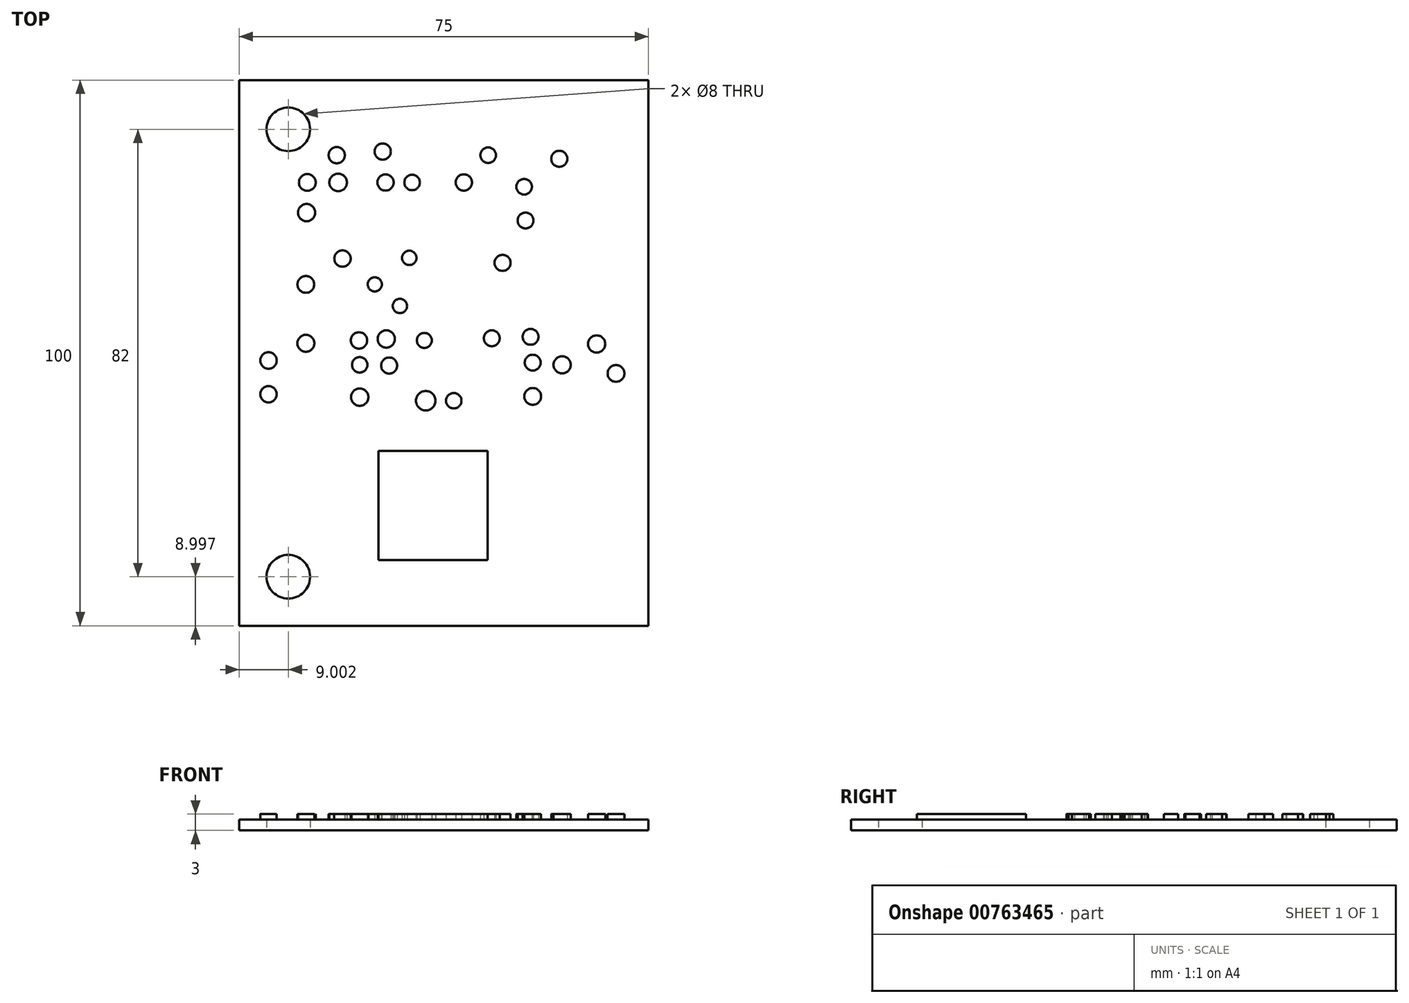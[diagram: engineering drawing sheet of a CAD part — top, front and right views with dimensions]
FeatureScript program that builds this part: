
annotation { "Feature Type Name" : "Feature", "Feature Type Description" : "" }
export const myFeature = defineFeature(function(context is Context, id is Id, definition is map)
    precondition{}
    {
        {
            var Q0;
            Q0=qCreatedBy(makeId("Top.planeOp"),FACE);
            var sketch = newSketch(context, id + "F0", { "sketchPlane" : qUnion([Q0])});
            skLineSegment(sketch, "E0.bottom", {"start": v(-62.6, 51.3) * mm, "end": v(12.4, 51.3) * mm});
            skLineSegment(sketch, "E0.top", {"start": v(-62.6, -48.7) * mm, "end": v(12.4, -48.7) * mm});
            skLineSegment(sketch, "E0.left", {"start": v(-62.6, 51.3) * mm, "end": v(-62.6, -48.7) * mm});
            skLineSegment(sketch, "E0.right", {"start": v(12.4, 51.3) * mm, "end": v(12.4, -48.7) * mm});
            skPoint(sketch, "E0.middle", {"position": v(-25.1, 1.3) * mm});
            skCircle(sketch, "E1", {"center": v(-53.6, 42.3) * mm, "radius": 4 * mm});
            skCircle(sketch, "E2", {"center": v(-53.6, -39.7) * mm, "radius": 4 * mm});
            skSolve(sketch);
        }
        {
            var Q0;
            Q0 = qSketchRegion(id + "F0", true);
            extrude(context, id + "F1", {"entities" : qUnion([Q0]), "depth" : 2 * mm, "offsetDistance" : 25 * mm});
        }
        {
            var Q0;
            Q0=makeQuery(id+"F1.opExtrude","CAP_FACE",FACE,{"disambiguationData":[OSD([sQuery(id+"F0.wireOp",EDGE,"E0.bottom"),sQuery(id+"F0.wireOp",EDGE,"E0.top"),sQuery(id+"F0.wireOp",EDGE,"E0.left"),sQuery(id+"F0.wireOp",EDGE,"E0.right"),sQuery(id+"F0.wireOp",EDGE,"E1"),sQuery(id+"F0.wireOp",EDGE,"E2")])],"isStart":false});
            var sketch = newSketch(context, id + "F2", { "sketchPlane" : qUnion([Q0])});
            skCircle(sketch, "E3", {"center": v(-44.72, 37.57) * mm, "radius": 1.49 * mm});
            skCircle(sketch, "E4", {"center": v(-44.46, 32.57) * mm, "radius": 1.6 * mm});
            skCircle(sketch, "E5", {"center": v(-50.12, 32.57) * mm, "radius": 1.53 * mm});
            skCircle(sketch, "E6", {"center": v(-50.25, 27.04) * mm, "radius": 1.58 * mm});
            skCircle(sketch, "E7", {"center": v(-30.9, 32.57) * mm, "radius": 1.42 * mm});
            skCircle(sketch, "E8", {"center": v(-35.78, 32.57) * mm, "radius": 1.49 * mm});
            skCircle(sketch, "E9", {"center": v(-36.3, 38.22) * mm, "radius": 1.49 * mm});
            skCircle(sketch, "E10", {"center": v(-21.43, 32.57) * mm, "radius": 1.5 * mm});
            skCircle(sketch, "E11", {"center": v(-16.96, 37.57) * mm, "radius": 1.42 * mm});
            skCircle(sketch, "E12", {"center": v(-10.12, 25.6) * mm, "radius": 1.45 * mm});
            skCircle(sketch, "E13", {"center": v(-10.38, 31.78) * mm, "radius": 1.42 * mm});
            skCircle(sketch, "E14", {"center": v(-3.93, 36.9) * mm, "radius": 1.47 * mm});
            skCircle(sketch, "E15", {"center": v(-50.38, 13.88) * mm, "radius": 1.53 * mm});
            skCircle(sketch, "E16", {"center": v(-43.67, 18.62) * mm, "radius": 1.5 * mm});
            skCircle(sketch, "E17", {"center": v(-33.14, 9.93) * mm, "radius": 1.32 * mm});
            skCircle(sketch, "E18", {"center": v(-37.75, 13.88) * mm, "radius": 1.3 * mm});
            skCircle(sketch, "E19", {"center": v(-31.43, 18.75) * mm, "radius": 1.32 * mm});
            skCircle(sketch, "E20", {"center": v(-14.33, 17.83) * mm, "radius": 1.47 * mm});
            skCircle(sketch, "E21", {"center": v(-57.22, -6.25) * mm, "radius": 1.5 * mm});
            skCircle(sketch, "E22", {"center": v(-57.22, -0.07) * mm, "radius": 1.51 * mm});
            skCircle(sketch, "E23", {"center": v(-50.38, 3.1) * mm, "radius": 1.55 * mm});
            skCircle(sketch, "E24", {"center": v(-40.51, -6.78) * mm, "radius": 1.59 * mm});
            skCircle(sketch, "E25", {"center": v(-40.51, -0.86) * mm, "radius": 1.42 * mm});
            skCircle(sketch, "E26", {"center": v(-40.64, 3.62) * mm, "radius": 1.5 * mm});
            skCircle(sketch, "E27", {"center": v(-35.64, 3.88) * mm, "radius": 1.58 * mm});
            skCircle(sketch, "E28", {"center": v(-35.12, -0.99) * mm, "radius": 1.47 * mm});
            skCircle(sketch, "E29", {"center": v(-28.4, -7.43) * mm, "radius": 1.79 * mm});
            skCircle(sketch, "E30", {"center": v(-23.28, -7.43) * mm, "radius": 1.42 * mm});
            skCircle(sketch, "E31", {"center": v(-28.67, 3.62) * mm, "radius": 1.37 * mm});
            skCircle(sketch, "E32", {"center": v(-16.3, 4.01) * mm, "radius": 1.45 * mm});
            skCircle(sketch, "E33", {"center": v(-9.2, 4.28) * mm, "radius": 1.45 * mm});
            skCircle(sketch, "E34", {"center": v(-8.8, -0.46) * mm, "radius": 1.45 * mm});
            skCircle(sketch, "E35", {"center": v(-8.8, -6.65) * mm, "radius": 1.54 * mm});
            skCircle(sketch, "E36", {"center": v(-3.4, -0.86) * mm, "radius": 1.58 * mm});
            skCircle(sketch, "E37", {"center": v(2.9, 2.96) * mm, "radius": 1.58 * mm});
            skCircle(sketch, "E38", {"center": v(6.46, -2.43) * mm, "radius": 1.53 * mm});
            skLineSegment(sketch, "E39.bottom", {"start": v(-37.1, -16.65) * mm, "end": v(-17.1, -16.65) * mm});
            skLineSegment(sketch, "E39.top", {"start": v(-37.1, -36.65) * mm, "end": v(-17.1, -36.65) * mm});
            skLineSegment(sketch, "E39.left", {"start": v(-37.1, -16.65) * mm, "end": v(-37.1, -36.65) * mm});
            skLineSegment(sketch, "E39.right", {"start": v(-17.1, -16.65) * mm, "end": v(-17.1, -36.65) * mm});
            skPoint(sketch, "E39.middle", {"position": v(-27.1, -26.65) * mm});
            skSolve(sketch);
        }
        {
            var Q0;
            Q0 = qSketchRegion(id + "F2", true);
            extrude(context, id + "F3", {"entities" : qUnion([Q0]), "operationType" : NewBodyOperationType.ADD, "depth" : 1 * mm, "offsetDistance" : 25 * mm});
        }
    });
